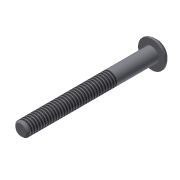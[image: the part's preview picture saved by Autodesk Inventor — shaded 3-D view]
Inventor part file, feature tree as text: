
AUTODESK INVENTOR PART (.ipt)
format: ipt  version: 2013 (Build 170138000, 138)  size: 124,416 bytes
history: native  units: in
note: dims shown in document units (in); Inventor stores cm internally (conversion verified against a paired STEP export)
features: sketch x3, extrude x2, revolve x1, chamfer x1, thread x1
ambient origin geometry x8: Origin, YZ Plane, XZ Plane, XY Plane, X Axis, Y Axis, Z Axis, Center Point
bodies: Solid1 (feature_tree)
feature tree (8):
  extrude  "Extrusion1"  Depth=1.5in TaperAngle=0.0deg
  revolve  "Revolution1"  [1 undecoded]
  extrude  "Extrusion2"  Depth=0.0938in
  chamfer  "Chamfer1"  Distance=0.0625in
  thread  "Thread1"  [1 undecoded]
  sketch  "Sketch1"  dims[d0=0.164in d1=1.5in d2=0.0in]
  sketch  "Sketch2"  dims[d3=0.087in d6=0.08in]
  sketch  "Sketch3"  dims[d7=90.0deg d8=0.0938in d9=0.0625in d10=0.0in d13=0.02in d14=0.125in d15=45.0deg d16=1.0in d17=0.0in d19=0.156in]
note: 2 required parameter values undecoded (feature->parameter linkage not recoverable at this tier; creation-order binding heuristic only, values carry confidence <= 0.55)